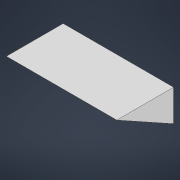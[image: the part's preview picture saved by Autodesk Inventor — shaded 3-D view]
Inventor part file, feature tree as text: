
AUTODESK INVENTOR PART (.ipt)
format: ipt  version: 2022 (Build 260153000, 153)  size: 92,672 bytes
history: native  units: in
note: dims shown in document units (in); Inventor stores cm internally (conversion verified against a paired STEP export)
features: extrude x2, sketch x2
ambient origin geometry x8: Origin, YZ Plane, XZ Plane, XY Plane, X Axis, Y Axis, Z Axis, Center Point
bodies: Solid1 (feature_tree)
feature tree (4):
  extrude  "Extrusion1"  Depth=13.7795in
  extrude  "Extrusion2"  TaperAngle=0.0deg  [1 undecoded]
  sketch  "Sketch1"  dims[d0=13.7795in d1=3.937in]
  sketch  "Sketch2"  dims[d2=7.0866in d3=0.0in d5=0.0in d6=0.0in d4=0.0197in]
note: 1 required parameter value undecoded (feature->parameter linkage not recoverable at this tier; creation-order binding heuristic only, values carry confidence <= 0.55)
